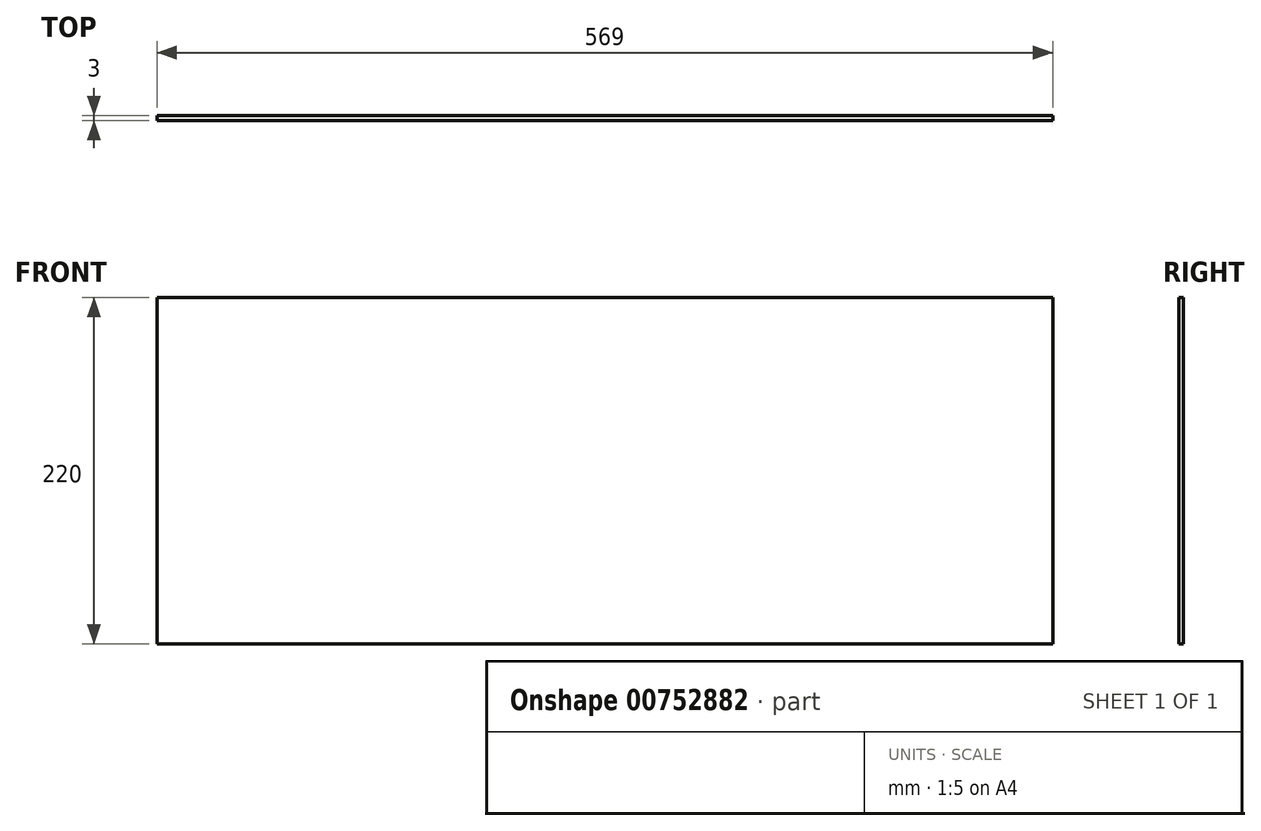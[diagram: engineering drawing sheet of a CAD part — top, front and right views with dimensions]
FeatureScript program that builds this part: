
annotation { "Feature Type Name" : "Feature", "Feature Type Description" : "" }
export const myFeature = defineFeature(function(context is Context, id is Id, definition is map)
    precondition{}
    {
        {
            var Q0;
            Q0=qCreatedBy(makeId("Front.planeOp"),FACE);
            var sketch = newSketch(context, id + "F0", { "sketchPlane" : qUnion([Q0])});
            skLineSegment(sketch, "E0.bottom", {"start": v(-284.5, 110) * mm, "end": v(284.5, 110) * mm});
            skLineSegment(sketch, "E0.top", {"start": v(-284.5, -110) * mm, "end": v(284.5, -110) * mm});
            skLineSegment(sketch, "E0.left", {"start": v(-284.5, 110) * mm, "end": v(-284.5, -110) * mm});
            skLineSegment(sketch, "E0.right", {"start": v(284.5, 110) * mm, "end": v(284.5, -110) * mm});
            skPoint(sketch, "E0.middle", {"position": v(0, 0) * mm});
            skSolve(sketch);
        }
        {
            var Q0;
            Q0=makeQuery(id+"F0.imprint","IMPRINT",FACE,{"disambiguationData":[TD([[makeQuery(id+"F0.imprint","IMPRINT",EDGE,{"derivedFrom":sQuery(id+"F0.wireOp",EDGE,"E0.bottom")}),-1.0]])]});
            extrude(context, id + "F1", {"entities" : qUnion([Q0]), "depth" : 3 * mm, "offsetDistance" : 25 * mm});
        }
    });
